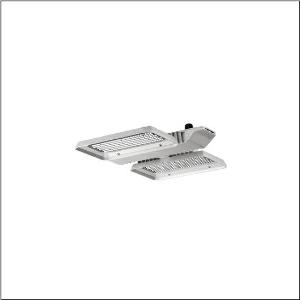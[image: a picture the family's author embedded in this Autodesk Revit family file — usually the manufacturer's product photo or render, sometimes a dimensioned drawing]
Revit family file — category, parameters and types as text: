
# Revit family: highbay_11_51hla2d14fca
name_source: partatom
category: Lighting Fixtures
units: mm (PartAtom-declared; Revit-internal decimal feet)

## family parameters
Cut with Voids When Loaded = No
Host = Face
Light Source = No
Part Type = Normal
Room Calculation Point = No
Round Connector Dimension = Use Diameter
Shared = No

## types (1)
- --- (1 x LED, 14400 lm, 81.2 W, 4000K)
    Apparent Load = 81 VA
    CIE Flux Codes = 89 96 99 100 100
    Color Rendering = 80
    Color Temperature = 4000K
    Default Elevation = 1800 mm
    Description = Highbay 11, LED high bay luminaire, primary light control with lens, of PMMA, light emission: direct distribution, primary light characteristic: symmetric, installation type: surface-mounted, suspended mounting, for 1x 2x LED, rated luminous flux: 14.400lm, luminous efficacy: 177lm/W, light colour: 840, colour temperature: 4000K, control gear: ECG DALI, with terminal, 5-pole, max. 2.5mm², mains connection: 230..240V, AC, 50/60Hz, rated input power: 81W, LED unit, of diecast aluminium, unplated, bead blasted, silver, length: 470mm, width: 500mm, height: 65mm, housing, of diecast aluminium, uncoated, bead blasted, silver, protection rating (complete): IP65, insulation class (complete): insulation class I (protective earthing), certification: CE, ENEC, VDE, UKCA, protection symbol: D, impact resistance: IK08 with glass or PC cover, permissible operating ambient temperature: -35..+55°C, reducing of maximum allowable ambient temperature of 5°C with ceiling mounting, corresponds to IFS (International Featured Standards) requirements for safety and quality in the food industry, packaging unit: 1 piece
    Height = 95 mm
    Lamp = 1 x LED
    Lamp Light Flux = 14400 lm
    Lamp Power = 81.2 W
    Lamp count = 1
    Length = 468 mm
    Luminous efficacy = 177 lm/W
    Manufacturer = Siteco
    ModVariant = No
    Model = 51HLA2D14FCA
    Mounting Place = Ceiling
    Mounting Type = Pendant
    Number of Poles = 1
    OnlyDefault = Yes
    Power Factor = 1
    Product Name = Highbay 11
    Product group = LED high bay luminaire
    ProductGroupID = 903
    Protection Class = Protection class I
    Protection Degree = IP 65
    RLX_Detail_Level = 1
    RLX_Emergency_Light_Flux = 0 lm
    RLX_Emergency_Type = 0
    RLX_Emergency_Type_DB = No
    RlxData = <blob elided: 86369 chars, md5=ad4dfad4>
    Socket = socket
    Standby Power = 0 W
    System Light Flux = 14400 lm
    System Power = 81 W
    Type Comments = factory setting: luminous flux: 100 % | dim-lin: 254 | 460 mA
    Type Image = l_1003425.jpg
    URL = http://relux.com
    VarID = @adj_146003
    Voltage = 0 V
    Weight = 0.00 kg
    Width = 501 mm

## geometry (parser evidence)
native form markers: Blend x4, Sweep x13
no freeform markers — native parametric forms only
